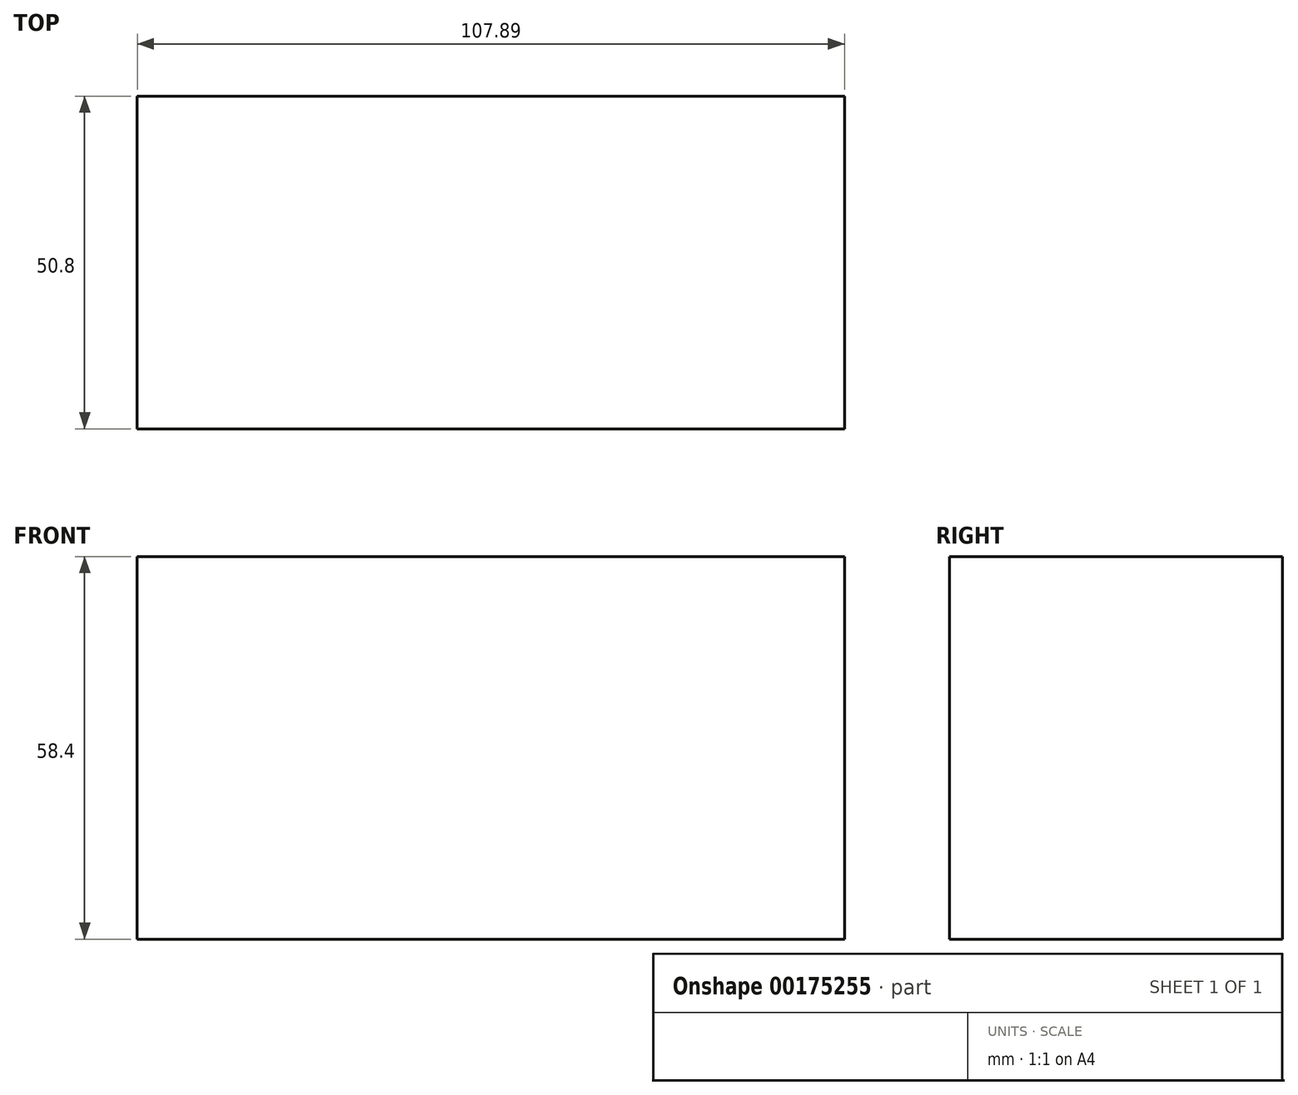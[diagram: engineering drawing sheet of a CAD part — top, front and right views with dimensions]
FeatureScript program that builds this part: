
annotation { "Feature Type Name" : "Feature", "Feature Type Description" : "" }
export const myFeature = defineFeature(function(context is Context, id is Id, definition is map)
    precondition{}
    {
        {
            var Q0;
            Q0=qCreatedBy(makeId("Front.planeOp"),FACE);
            var sketch = newSketch(context, id + "F0", { "sketchPlane" : qUnion([Q0])});
            skLineSegment(sketch, "E0.bottom", {"start": v(-51.5, 29.87) * mm, "end": v(56.4, 29.87) * mm});
            skLineSegment(sketch, "E0.top", {"start": v(-51.5, -28.53) * mm, "end": v(56.4, -28.53) * mm});
            skLineSegment(sketch, "E0.left", {"start": v(-51.5, 29.87) * mm, "end": v(-51.5, -28.53) * mm});
            skLineSegment(sketch, "E0.right", {"start": v(56.4, 29.87) * mm, "end": v(56.4, -28.53) * mm});
            skSolve(sketch);
        }
        {
            var Q0;
            Q0 = qSketchRegion(id + "F0", true);
            extrude(context, id + "F1", {"entities" : qUnion([Q0]), "depth" : 50.8 * mm});
        }
        {
            var Q0;
            Q0=makeQuery(id+"F1.opExtrude","SWEPT_FACE",FACE,{"disambiguationData":[OSD([sQuery(id+"F0.wireOp",EDGE,"E0.top")])]});
            shell(context, id + "F2", {"entities" : qUnion([Q0]), "thickness" : 25.4 * mm});
        }
    });
